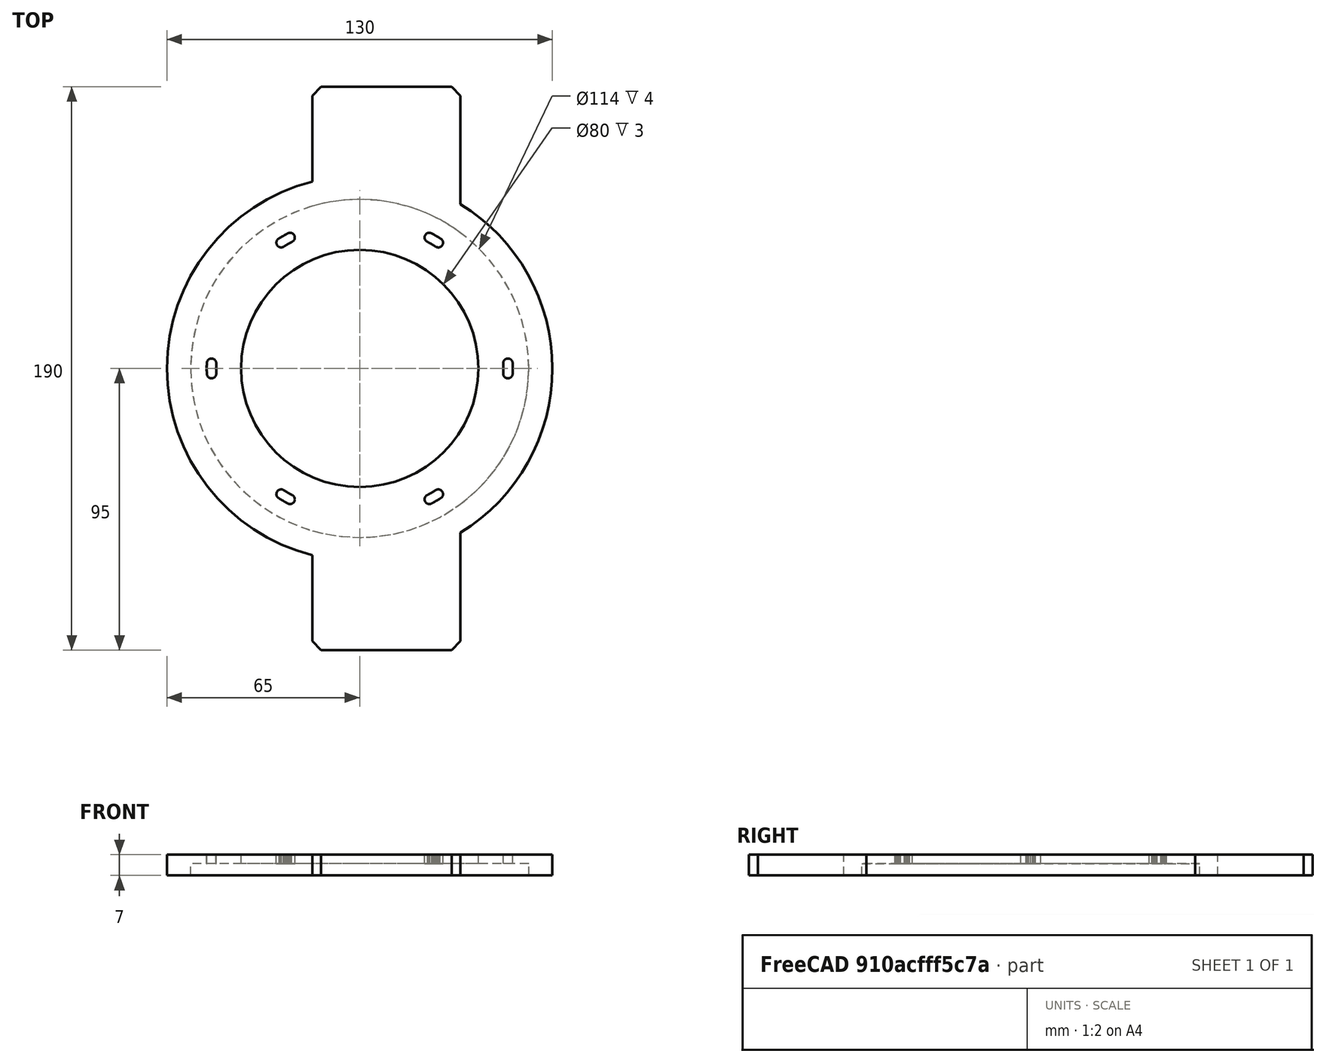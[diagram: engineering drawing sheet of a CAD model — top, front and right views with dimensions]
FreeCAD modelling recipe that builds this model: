
FCSTD DOCUMENT  (FreeCAD 0.15R4671 (Git))
Label: table_flat_mount
License: All rights reserved
LicenseURL: http://en.wikipedia.org/wiki/All_rights_reserved
objects: Part::Cylinder×51, Part::MultiFuse×30, Part::Cut×2, Part::Box×1, Part::Mirroring×1, Part::Chamfer×1
note: 86 computed .brp shape members not serialized (recipe doc carries the construction recipe); baked Part::Feature solids carry a one-line shape summary decoded from their .brp

FEATURE [Part::Cylinder] Cylinder
  Angle = 360
  Height = 7
  Radius = 65
FEATURE [Part::Box] Box  label="Cube"
  Height = 7
  Length = 50
  Placement = pos=(-16,45,0) rot=(0,0,1;0rad)
  Width = 50
FEATURE [Part::Mirroring] Part__Mirroring  label="Cube (Mirror #1)"
  Base = (0,0,0)
  Normal = (0,1,0)
  Source = -> Box
FEATURE [Part::Cylinder] Cylinder001
  Angle = 360
  Height = 10
  Placement = pos=(50,0,-2) rot=(0,0,1;0rad)
  Radius = 1.6
FEATURE [Part::Cylinder] Cylinder002
  Angle = 360
  Height = 10
  Placement = pos=(-50,0,-2) rot=(0,0,1;0rad)
  Radius = 1.6
FEATURE [Part::MultiFuse] Fusion
  Placement = pos=(0,0,0) rot=(0,0,1;0.017453rad)
  Shapes = -> [Cylinder001,Cylinder002]
FEATURE [Part::Cylinder] Cylinder003
  Angle = 360
  Height = 10
  Placement = pos=(50,0,-2) rot=(0,0,1;0rad)
  Radius = 1.6
FEATURE [Part::Cylinder] Cylinder004
  Angle = 360
  Height = 10
  Placement = pos=(-50,0,-2) rot=(0,0,1;0rad)
  Radius = 1.6
FEATURE [Part::MultiFuse] Fusion001
  Placement = pos=(0,0,0) rot=(0,0,1;0.034907rad)
  Shapes = -> [Cylinder003,Cylinder004]
FEATURE [Part::Cylinder] Cylinder005
  Angle = 360
  Height = 10
  Placement = pos=(50,0,-2) rot=(0,0,1;0rad)
  Radius = 1.6
FEATURE [Part::Cylinder] Cylinder006
  Angle = 360
  Height = 10
  Placement = pos=(-50,0,-2) rot=(0,0,1;0rad)
  Radius = 1.6
FEATURE [Part::MultiFuse] Fusion002
  Placement = pos=(0,0,0) rot=(0,0,-1;0.017453rad)
  Shapes = -> [Cylinder005,Cylinder006]
FEATURE [Part::Cylinder] Cylinder007
  Angle = 360
  Height = 10
  Placement = pos=(50,0,-2) rot=(0,0,1;0rad)
  Radius = 1.6
FEATURE [Part::Cylinder] Cylinder008
  Angle = 360
  Height = 10
  Placement = pos=(-50,0,-2) rot=(0,0,1;0rad)
  Radius = 1.6
FEATURE [Part::MultiFuse] Fusion003
  Placement = pos=(0,0,0) rot=(0,0,-1;0.034907rad)
  Shapes = -> [Cylinder007,Cylinder008]
FEATURE [Part::Cylinder] Cylinder009
  Angle = 360
  Height = 10
  Placement = pos=(50,0,-2) rot=(0,0,1;0rad)
  Radius = 1.6
FEATURE [Part::Cylinder] Cylinder010
  Angle = 360
  Height = 10
  Placement = pos=(-50,0,-2) rot=(0,0,1;0rad)
  Radius = 1.6
FEATURE [Part::MultiFuse] Fusion004
  Placement = pos=(0,0,0) rot=(0,0,-1;0.008727rad)
  Shapes = -> [Cylinder009,Cylinder010]
FEATURE [Part::Cylinder] Cylinder011
  Angle = 360
  Height = 10
  Placement = pos=(50,0,-2) rot=(0,0,1;0rad)
  Radius = 1.6
FEATURE [Part::Cylinder] Cylinder012
  Angle = 360
  Height = 10
  Placement = pos=(-50,0,-2) rot=(0,0,1;0rad)
  Radius = 1.6
FEATURE [Part::MultiFuse] Fusion005
  Placement = pos=(0,0,0) rot=(0,0,-1;0.02618rad)
  Shapes = -> [Cylinder011,Cylinder012]
FEATURE [Part::Cylinder] Cylinder013
  Angle = 360
  Height = 10
  Placement = pos=(50,0,-2) rot=(0,0,1;0rad)
  Radius = 1.6
FEATURE [Part::Cylinder] Cylinder014
  Angle = 360
  Height = 10
  Placement = pos=(-50,0,-2) rot=(0,0,1;0rad)
  Radius = 1.6
FEATURE [Part::MultiFuse] Fusion006
  Placement = pos=(0,0,0) rot=(0,0,1;0.02618rad)
  Shapes = -> [Cylinder013,Cylinder014]
FEATURE [Part::Cylinder] Cylinder015
  Angle = 360
  Height = 10
  Placement = pos=(50,0,-2) rot=(0,0,1;0rad)
  Radius = 1.6
FEATURE [Part::Cylinder] Cylinder016
  Angle = 360
  Height = 10
  Placement = pos=(-50,0,-2) rot=(0,0,1;0rad)
  Radius = 1.6
FEATURE [Part::MultiFuse] Fusion007
  Placement = pos=(0,0,0) rot=(0,0,1;0.008727rad)
  Shapes = -> [Cylinder015,Cylinder016]
FEATURE [Part::MultiFuse] Fusion008
  Shapes = -> [Fusion003,Fusion006,Fusion001,Fusion005,Fusion002,Fusion004,Fusion,Fusion007]
FEATURE [Part::Cylinder] Cylinder017
  Angle = 360
  Height = 10
  Placement = pos=(50,0,-2) rot=(0,0,1;0rad)
  Radius = 1.6
FEATURE [Part::Cylinder] Cylinder018
  Angle = 360
  Height = 10
  Placement = pos=(-50,0,-2) rot=(0,0,1;0rad)
  Radius = 1.6
FEATURE [Part::MultiFuse] Fusion009
  Placement = pos=(0,0,0) rot=(0,0,1;0.017453rad)
  Shapes = -> [Cylinder017,Cylinder018]
FEATURE [Part::Cylinder] Cylinder019
  Angle = 360
  Height = 10
  Placement = pos=(50,0,-2) rot=(0,0,1;0rad)
  Radius = 1.6
FEATURE [Part::Cylinder] Cylinder020
  Angle = 360
  Height = 10
  Placement = pos=(-50,0,-2) rot=(0,0,1;0rad)
  Radius = 1.6
FEATURE [Part::MultiFuse] Fusion010
  Placement = pos=(0,0,0) rot=(0,0,1;0.034907rad)
  Shapes = -> [Cylinder019,Cylinder020]
FEATURE [Part::Cylinder] Cylinder021
  Angle = 360
  Height = 10
  Placement = pos=(50,0,-2) rot=(0,0,1;0rad)
  Radius = 1.6
FEATURE [Part::Cylinder] Cylinder022
  Angle = 360
  Height = 10
  Placement = pos=(-50,0,-2) rot=(0,0,1;0rad)
  Radius = 1.6
FEATURE [Part::MultiFuse] Fusion011
  Placement = pos=(0,0,0) rot=(0,0,-1;0.017453rad)
  Shapes = -> [Cylinder021,Cylinder022]
FEATURE [Part::Cylinder] Cylinder023
  Angle = 360
  Height = 10
  Placement = pos=(50,0,-2) rot=(0,0,1;0rad)
  Radius = 1.6
FEATURE [Part::Cylinder] Cylinder024
  Angle = 360
  Height = 10
  Placement = pos=(-50,0,-2) rot=(0,0,1;0rad)
  Radius = 1.6
FEATURE [Part::MultiFuse] Fusion012
  Placement = pos=(0,0,0) rot=(0,0,-1;0.034907rad)
  Shapes = -> [Cylinder023,Cylinder024]
FEATURE [Part::Cylinder] Cylinder025
  Angle = 360
  Height = 10
  Placement = pos=(50,0,-2) rot=(0,0,1;0rad)
  Radius = 1.6
FEATURE [Part::Cylinder] Cylinder026
  Angle = 360
  Height = 10
  Placement = pos=(-50,0,-2) rot=(0,0,1;0rad)
  Radius = 1.6
FEATURE [Part::MultiFuse] Fusion013
  Placement = pos=(0,0,0) rot=(0,0,-1;0.008727rad)
  Shapes = -> [Cylinder025,Cylinder026]
FEATURE [Part::Cylinder] Cylinder027
  Angle = 360
  Height = 10
  Placement = pos=(50,0,-2) rot=(0,0,1;0rad)
  Radius = 1.6
FEATURE [Part::Cylinder] Cylinder028
  Angle = 360
  Height = 10
  Placement = pos=(-50,0,-2) rot=(0,0,1;0rad)
  Radius = 1.6
FEATURE [Part::MultiFuse] Fusion014
  Placement = pos=(0,0,0) rot=(0,0,-1;0.02618rad)
  Shapes = -> [Cylinder027,Cylinder028]
FEATURE [Part::Cylinder] Cylinder029
  Angle = 360
  Height = 10
  Placement = pos=(50,0,-2) rot=(0,0,1;0rad)
  Radius = 1.6
FEATURE [Part::Cylinder] Cylinder030
  Angle = 360
  Height = 10
  Placement = pos=(-50,0,-2) rot=(0,0,1;0rad)
  Radius = 1.6
FEATURE [Part::MultiFuse] Fusion015
  Placement = pos=(0,0,0) rot=(0,0,1;0.02618rad)
  Shapes = -> [Cylinder029,Cylinder030]
FEATURE [Part::Cylinder] Cylinder031
  Angle = 360
  Height = 10
  Placement = pos=(50,0,-2) rot=(0,0,1;0rad)
  Radius = 1.6
FEATURE [Part::Cylinder] Cylinder032
  Angle = 360
  Height = 10
  Placement = pos=(-50,0,-2) rot=(0,0,1;0rad)
  Radius = 1.6
FEATURE [Part::MultiFuse] Fusion016
  Placement = pos=(0,0,0) rot=(0,0,1;0.008727rad)
  Shapes = -> [Cylinder031,Cylinder032]
FEATURE [Part::MultiFuse] Fusion017
  Placement = pos=(0,0,0) rot=(0,0,1;1.0472rad)
  Shapes = -> [Fusion012,Fusion015,Fusion010,Fusion014,Fusion011,Fusion013,Fusion009,Fusion016]
FEATURE [Part::Cylinder] Cylinder033
  Angle = 360
  Height = 10
  Placement = pos=(50,0,-2) rot=(0,0,1;0rad)
  Radius = 1.6
FEATURE [Part::Cylinder] Cylinder034
  Angle = 360
  Height = 10
  Placement = pos=(-50,0,-2) rot=(0,0,1;0rad)
  Radius = 1.6
FEATURE [Part::MultiFuse] Fusion018
  Placement = pos=(0,0,0) rot=(0,0,1;0.017453rad)
  Shapes = -> [Cylinder033,Cylinder034]
FEATURE [Part::Cylinder] Cylinder035
  Angle = 360
  Height = 10
  Placement = pos=(50,0,-2) rot=(0,0,1;0rad)
  Radius = 1.6
FEATURE [Part::Cylinder] Cylinder036
  Angle = 360
  Height = 10
  Placement = pos=(-50,0,-2) rot=(0,0,1;0rad)
  Radius = 1.6
FEATURE [Part::MultiFuse] Fusion019
  Placement = pos=(0,0,0) rot=(0,0,1;0.034907rad)
  Shapes = -> [Cylinder035,Cylinder036]
FEATURE [Part::Cylinder] Cylinder037
  Angle = 360
  Height = 10
  Placement = pos=(50,0,-2) rot=(0,0,1;0rad)
  Radius = 1.6
FEATURE [Part::Cylinder] Cylinder038
  Angle = 360
  Height = 10
  Placement = pos=(-50,0,-2) rot=(0,0,1;0rad)
  Radius = 1.6
FEATURE [Part::MultiFuse] Fusion020
  Placement = pos=(0,0,0) rot=(0,0,-1;0.017453rad)
  Shapes = -> [Cylinder037,Cylinder038]
FEATURE [Part::Cylinder] Cylinder039
  Angle = 360
  Height = 10
  Placement = pos=(50,0,-2) rot=(0,0,1;0rad)
  Radius = 1.6
FEATURE [Part::Cylinder] Cylinder040
  Angle = 360
  Height = 10
  Placement = pos=(-50,0,-2) rot=(0,0,1;0rad)
  Radius = 1.6
FEATURE [Part::MultiFuse] Fusion021
  Placement = pos=(0,0,0) rot=(0,0,-1;0.034907rad)
  Shapes = -> [Cylinder039,Cylinder040]
FEATURE [Part::Cylinder] Cylinder041
  Angle = 360
  Height = 10
  Placement = pos=(50,0,-2) rot=(0,0,1;0rad)
  Radius = 1.6
FEATURE [Part::Cylinder] Cylinder042
  Angle = 360
  Height = 10
  Placement = pos=(-50,0,-2) rot=(0,0,1;0rad)
  Radius = 1.6
FEATURE [Part::MultiFuse] Fusion022
  Placement = pos=(0,0,0) rot=(0,0,-1;0.008727rad)
  Shapes = -> [Cylinder041,Cylinder042]
FEATURE [Part::Cylinder] Cylinder043
  Angle = 360
  Height = 10
  Placement = pos=(50,0,-2) rot=(0,0,1;0rad)
  Radius = 1.6
FEATURE [Part::Cylinder] Cylinder044
  Angle = 360
  Height = 10
  Placement = pos=(-50,0,-2) rot=(0,0,1;0rad)
  Radius = 1.6
FEATURE [Part::MultiFuse] Fusion023
  Placement = pos=(0,0,0) rot=(0,0,-1;0.02618rad)
  Shapes = -> [Cylinder043,Cylinder044]
FEATURE [Part::Cylinder] Cylinder045
  Angle = 360
  Height = 10
  Placement = pos=(50,0,-2) rot=(0,0,1;0rad)
  Radius = 1.6
FEATURE [Part::Cylinder] Cylinder046
  Angle = 360
  Height = 10
  Placement = pos=(-50,0,-2) rot=(0,0,1;0rad)
  Radius = 1.6
FEATURE [Part::MultiFuse] Fusion024
  Placement = pos=(0,0,0) rot=(0,0,1;0.02618rad)
  Shapes = -> [Cylinder045,Cylinder046]
FEATURE [Part::Cylinder] Cylinder047
  Angle = 360
  Height = 10
  Placement = pos=(50,0,-2) rot=(0,0,1;0rad)
  Radius = 1.6
FEATURE [Part::Cylinder] Cylinder048
  Angle = 360
  Height = 10
  Placement = pos=(-50,0,-2) rot=(0,0,1;0rad)
  Radius = 1.6
FEATURE [Part::MultiFuse] Fusion025
  Placement = pos=(0,0,0) rot=(0,0,1;0.008727rad)
  Shapes = -> [Cylinder047,Cylinder048]
FEATURE [Part::MultiFuse] Fusion026
  Placement = pos=(0,0,0) rot=(0,0,1;2.0944rad)
  Shapes = -> [Fusion021,Fusion024,Fusion019,Fusion023,Fusion020,Fusion022,Fusion018,Fusion025]
FEATURE [Part::MultiFuse] Fusion027
  Shapes = -> [Fusion026,Fusion017,Fusion008]
FEATURE [Part::Cylinder] Cylinder049
  Angle = 360
  Height = 4
  Radius = 57
FEATURE [Part::Cylinder] Cylinder050
  Angle = 360
  Height = 7
  Radius = 40
FEATURE [Part::MultiFuse] Fusion028
  Shapes = -> [Cylinder050,Cylinder049]
FEATURE [Part::MultiFuse] Fusion029
  Shapes = -> [Cylinder,Part__Mirroring,Box]
FEATURE [Part::Cut] Cut
  Base = -> Fusion029
  Tool = -> Fusion028
FEATURE [Part::Cut] Cut001
  Base = -> Cut
  Tool = -> Fusion027
FEATURE [Part::Chamfer] Chamfer
  Base = -> Cut001
  Edges = 4 edges r=3: [Edge2,Edge4,Edge190,Edge449]
